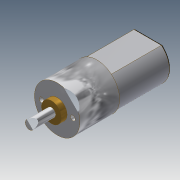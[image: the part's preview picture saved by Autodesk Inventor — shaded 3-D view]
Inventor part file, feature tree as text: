
AUTODESK INVENTOR PART (.ipt)
format: ipt  version: 2014 SP1 (Build 180222100, 222)  size: 151,040 bytes
history: native  units: in
note: dims shown in document units (in); Inventor stores cm internally (conversion verified against a paired STEP export)
features: extrude x6, sketch x6, fillet x1
ambient origin geometry x8: Origin, YZ Plane, XZ Plane, XY Plane, X Axis, Y Axis, Z Axis, Center Point
bodies: Solid1 (feature_tree)
feature tree (13):
  extrude  "Extrusion1"  Depth=0.5512in TaperAngle=0.0deg
  extrude  "Extrusion2"  Depth=0.0669in
  extrude  "Extrusion3"  Depth=0.2165in
  extrude  "Extrusion4"  Depth=0.3937in
  extrude  "Extrusion5"  Depth=0.1181in
  fillet  "Fillet1"  Radius=0.3051in
  extrude  "Extrusion6"  Depth=0.0197in
  sketch  "Sketch1"  dims[d0=0.6299in d1=0.5512in d2=0.0in]
  sketch  "Sketch2"  dims[d3=0.0669in d4=0.0669in]
  sketch  "Sketch3"  dims[d5=0.2165in d6=0.2165in]
  sketch  "Sketch4"  dims[d7=0.3937in d8=0.0in d9=0.2756in]
  sketch  "Sketch5"  dims[d10=0.0787in d11=0.0in d12=0.1181in d13=0.3051in d14=0.0in]
  sketch  "Sketch6"  dims[d15=0.6004in d16=0.2323in d17=0.2323in d18=0.7244in d19=0.0in d20=0.0197in d21=0.1969in d22=0.0197in d23=0.0in]
